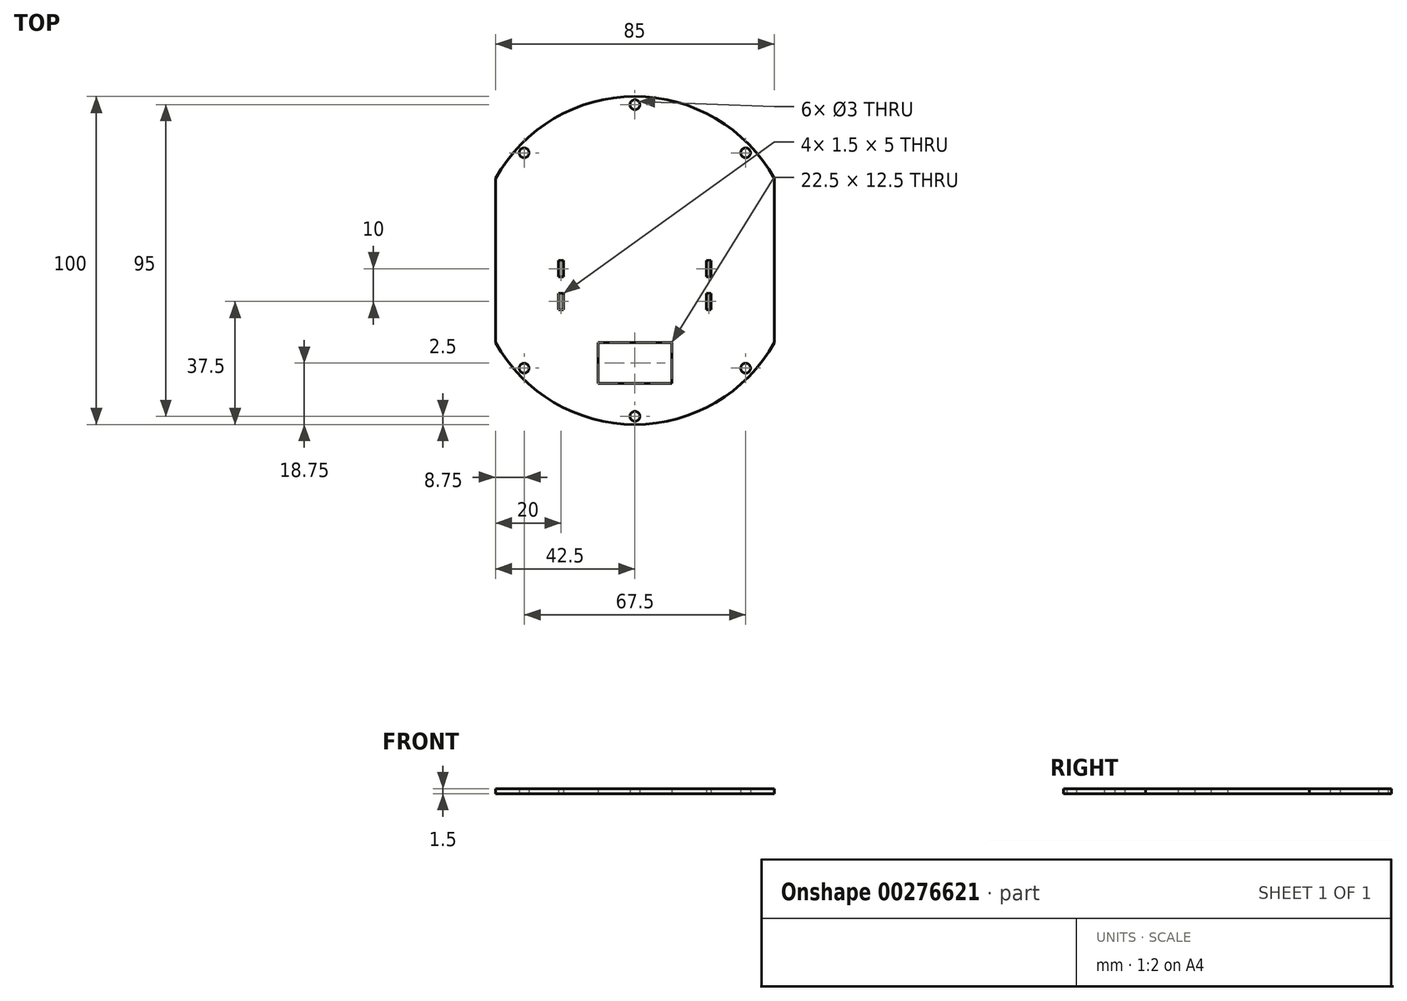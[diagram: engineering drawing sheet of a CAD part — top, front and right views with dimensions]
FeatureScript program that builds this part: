
annotation { "Feature Type Name" : "Feature", "Feature Type Description" : "" }
export const myFeature = defineFeature(function(context is Context, id is Id, definition is map)
    precondition{}
    {
        {
            var Q0;
            Q0=qCreatedBy(makeId("Top.planeOp"),FACE);
            var sketch = newSketch(context, id + "F0", { "sketchPlane" : qUnion([Q0])});
            skLineSegment(sketch, "E0.bottom", {"start": v(42.5, 25) * mm, "end": v(-42.5, 25) * mm, "construction": true});
            skLineSegment(sketch, "E0.top", {"start": v(42.5, -25) * mm, "end": v(-42.5, -25) * mm, "construction": true});
            skLineSegment(sketch, "E0.left", {"start": v(42.5, 25) * mm, "end": v(42.5, -25) * mm});
            skLineSegment(sketch, "E0.right", {"start": v(-42.5, 25) * mm, "end": v(-42.5, -25) * mm});
            skPoint(sketch, "E0.middle", {"position": v(0, 0) * mm});
            skLineSegment(sketch, "E1", {"start": v(0, 0) * mm, "end": v(0, 50) * mm, "construction": true});
            skArc(sketch, "E2", {"start": v(42.5, 25) * mm, "mid": v(0, 50) * mm, "end": v(-42.5, 25) * mm});
            skLineSegment(sketch, "E3", {"start": v(0, 0) * mm, "end": v(-42.5, 0) * mm, "construction": true});
            skArc(sketch, "E4.MirrorCS", {"start": v(42.5, -25) * mm, "mid": v(0, -50) * mm, "end": v(-42.5, -25) * mm});
            skArc(sketch, "E5.0", {"start": v(39.62, 25) * mm, "mid": v(0, 47.5) * mm, "end": v(-39.62, 25) * mm, "construction": true});
            skCircle(sketch, "E6", {"center": v(0, 47.5) * mm, "radius": 1.5 * mm});
            skCircle(sketch, "E7", {"center": v(-33.75, 32.81) * mm, "radius": 1.5 * mm});
            skCircle(sketch, "E8.MirrorC", {"center": v(33.75, 32.81) * mm, "radius": 1.5 * mm});
            skCircle(sketch, "E9.MirrorC", {"center": v(-33.75, -32.81) * mm, "radius": 1.5 * mm});
            skCircle(sketch, "E10.MirrorC", {"center": v(0, -47.5) * mm, "radius": 1.5 * mm});
            skCircle(sketch, "E11.MirrorC", {"center": v(33.75, -32.81) * mm, "radius": 1.5 * mm});
            skLineSegment(sketch, "E12.bottom", {"start": v(23.25, 0) * mm, "end": v(21.75, 0) * mm});
            skLineSegment(sketch, "E12.top", {"start": v(23.25, -5) * mm, "end": v(21.75, -5) * mm});
            skLineSegment(sketch, "E12.left", {"start": v(23.25, 0) * mm, "end": v(23.25, -5) * mm});
            skLineSegment(sketch, "E12.right", {"start": v(21.75, 0) * mm, "end": v(21.75, -5) * mm});
            skPoint(sketch, "E12.middle", {"position": v(22.5, -2.5) * mm});
            skLineSegment(sketch, "E13.1.0.0", {"start": v(21.75, -10) * mm, "end": v(21.75, -15) * mm});
            skLineSegment(sketch, "E13.1.0.1", {"start": v(23.25, -15) * mm, "end": v(21.75, -15) * mm});
            skPoint(sketch, "E13.1.0.2", {"position": v(22.5, -12.5) * mm});
            skLineSegment(sketch, "E13.1.0.3", {"start": v(23.25, -10) * mm, "end": v(21.75, -10) * mm});
            skLineSegment(sketch, "E13.1.0.4", {"start": v(23.25, -10) * mm, "end": v(23.25, -15) * mm});
            skLineSegment(sketch, "E13.direction1", {"start": v(21.75, -5) * mm, "end": v(21.75, -15) * mm, "construction": true});
            skLineSegment(sketch, "E14.MirrorCS", {"start": v(-21.75, 0) * mm, "end": v(-21.75, -5) * mm});
            skLineSegment(sketch, "E15.MirrorCS", {"start": v(-23.25, 0) * mm, "end": v(-21.75, 0) * mm});
            skLineSegment(sketch, "E16.MirrorCS", {"start": v(-23.25, 0) * mm, "end": v(-23.25, -5) * mm});
            skLineSegment(sketch, "E17.MirrorCS", {"start": v(-23.25, -5) * mm, "end": v(-21.75, -5) * mm});
            skLineSegment(sketch, "E18.MirrorCS", {"start": v(-23.25, -10) * mm, "end": v(-21.75, -10) * mm});
            skLineSegment(sketch, "E19.MirrorCS", {"start": v(-23.25, -15) * mm, "end": v(-21.75, -15) * mm});
            skLineSegment(sketch, "E20.MirrorCS", {"start": v(-23.25, -10) * mm, "end": v(-23.25, -15) * mm});
            skLineSegment(sketch, "E21.MirrorCS", {"start": v(-21.75, -5) * mm, "end": v(-21.75, -15) * mm, "construction": true});
            skLineSegment(sketch, "E22.MirrorCS", {"start": v(-21.75, -10) * mm, "end": v(-21.75, -15) * mm});
            skLineSegment(sketch, "E23.bottom", {"start": v(11.25, -37.5) * mm, "end": v(-11.25, -37.5) * mm});
            skLineSegment(sketch, "E23.top", {"start": v(11.25, -25) * mm, "end": v(-11.25, -25) * mm});
            skLineSegment(sketch, "E23.left", {"start": v(11.25, -37.5) * mm, "end": v(11.25, -25) * mm});
            skLineSegment(sketch, "E23.right", {"start": v(-11.25, -37.5) * mm, "end": v(-11.25, -25) * mm});
            skPoint(sketch, "E23.middle", {"position": v(0, -31.25) * mm});
            skSolve(sketch);
        }
        {
            var Q0;
            Q0 = qSketchRegion(id + "F0", true);
            extrude(context, id + "F1", {"entities" : qUnion([Q0]), "depth" : 1.5 * mm});
        }
    });
